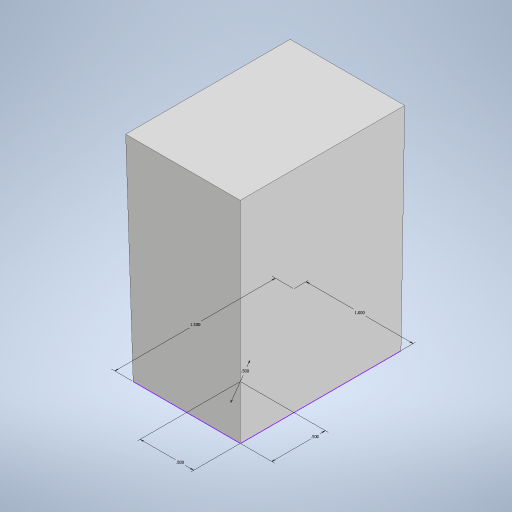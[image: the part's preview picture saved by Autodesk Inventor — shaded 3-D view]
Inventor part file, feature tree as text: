
AUTODESK INVENTOR PART (.ipt)
format: ipt  version: 2023 (Build 270158000, 158)  size: 206,336 bytes
history: native  units: in
note: dims shown in document units (in); Inventor stores cm internally (conversion verified against a paired STEP export)
features: sketch x1, extrude x1, draft x1
ambient origin geometry x8: Origin, YZ Plane, XZ Plane, XY Plane, X Axis, Y Axis, Z Axis, Center Point
bodies: Solid1 (feature_tree)
feature tree (3):
  sketch  "Sketch1"  dims[d0=0.5in d1=1.0in d2=1.5in d3=0.5in d4=0.5in d5=2.0in d6=0.0in d20=0.0069in]
  extrude  "Extrusion1"  Depth=2.0in
  draft  "FaceDraft1"
